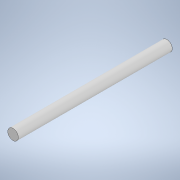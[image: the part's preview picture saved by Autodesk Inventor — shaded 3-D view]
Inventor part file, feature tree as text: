
AUTODESK INVENTOR PART (.ipt)
format: ipt  version: 2021 (Build 250183000, 183)  size: 91,648 bytes
history: native  units: mm
features: extrude x1, sketch x1
ambient origin geometry x8: Origin, YZ Plane, XZ Plane, XY Plane, X Axis, Y Axis, Z Axis, Center Point
bodies: Solid1 (feature_tree)
feature tree (2):
  extrude  "Extrusion1"  Depth=43.5mm TaperAngle=0.0deg
  sketch  "Sketch1"  dims[d0=3.0mm d1=43.5mm d2=0.0mm]
